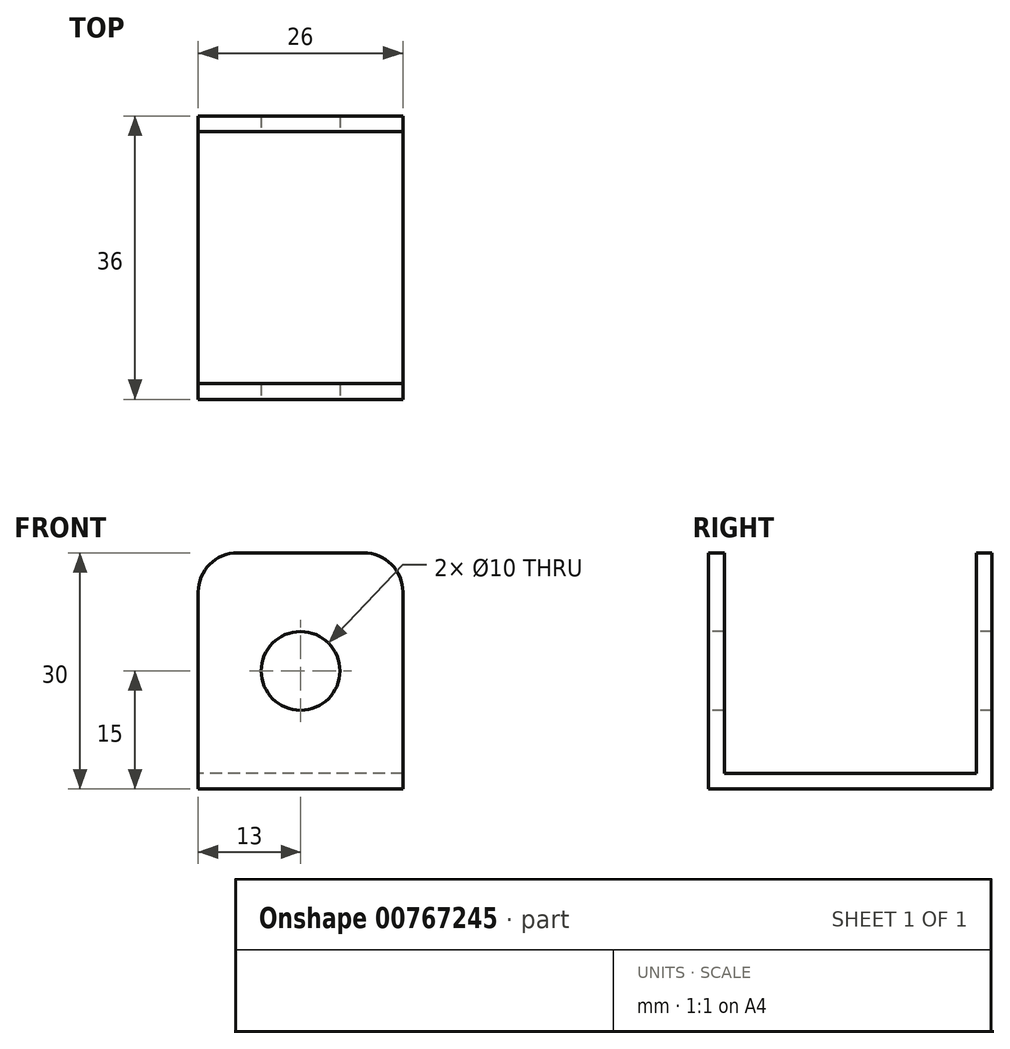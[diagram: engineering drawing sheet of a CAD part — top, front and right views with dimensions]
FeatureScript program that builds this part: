
annotation { "Feature Type Name" : "Feature", "Feature Type Description" : "" }
export const myFeature = defineFeature(function(context is Context, id is Id, definition is map)
    precondition{}
    {
        {
            var Q0;
            Q0=qCreatedBy(makeId("Right.planeOp"),FACE);
            var sketch = newSketch(context, id + "F0", { "sketchPlane" : qUnion([Q0])});
            skLineSegment(sketch, "E0.bottom", {"start": v(18, 15) * mm, "end": v(16, 15) * mm});
            skLineSegment(sketch, "E0.top", {"start": v(18, -15) * mm, "end": v(-18, -15) * mm});
            skLineSegment(sketch, "E0.left", {"start": v(18, 15) * mm, "end": v(18, -15) * mm});
            skLineSegment(sketch, "E0.right", {"start": v(-18, 15) * mm, "end": v(-18, -15) * mm});
            skPoint(sketch, "E0.middle", {"position": v(0, 0) * mm});
            skLineSegment(sketch, "E1.top", {"start": v(-16, -13) * mm, "end": v(16, -13) * mm});
            skLineSegment(sketch, "E1.left", {"start": v(-16, 15) * mm, "end": v(-16, -13) * mm});
            skLineSegment(sketch, "E1.right", {"start": v(16, 15) * mm, "end": v(16, -13) * mm});
            skLineSegment(sketch, "E2.trimOffspring", {"start": v(-16, 15) * mm, "end": v(-18, 15) * mm});
            skSolve(sketch);
        }
        {
            var Q0;
            Q0 = qSketchRegion(id + "F0", true);
            extrude(context, id + "F1", {"entities" : qUnion([Q0]), "endBound" : BoundingType.SYMMETRIC, "depth" : 26 * mm, "offsetDistance" : 25 * mm});
        }
        {
            var Q0;
            Q0=makeQuery(id+"F1.opExtrude","SWEPT_FACE",FACE,{"disambiguationData":[OSD([sQuery(id+"F0.wireOp",EDGE,"E0.right")])]});
            var sketch = newSketch(context, id + "F2", { "sketchPlane" : qUnion([Q0])});
            skCircle(sketch, "E3", {"center": v(0, 0) * mm, "radius": 5 * mm});
            skSolve(sketch);
        }
        {
            var Q0;
            Q0=makeQuery(id+"F2.imprint","IMPRINT",FACE,{"disambiguationData":[TD([[makeQuery(id+"F2.imprint","IMPRINT",EDGE,{"derivedFrom":sQuery(id+"F2.wireOp",EDGE,"E3")}),1.0]])]});
            extrude(context, id + "F3", {"entities" : qUnion([Q0]), "operationType" : NewBodyOperationType.REMOVE, "endBound" : BoundingType.THROUGH_ALL, "oppositeDirection" : true, "depth" : 25 * mm, "offsetDistance" : 25 * mm});
        }
        {
            var Q0;
            Q0=makeQuery(id+"F1.opExtrude","CAP_EDGE",EDGE,{"disambiguationData":[OSD([sQuery(id+"F0.wireOp",EDGE,"E2.trimOffspring")])],"isStart":false});
            var Q1;
            Q1=makeQuery(id+"F1.opExtrude","CAP_EDGE",EDGE,{"disambiguationData":[OSD([sQuery(id+"F0.wireOp",EDGE,"E2.trimOffspring")])],"isStart":true});
            var Q2;
            Q2=makeQuery(id+"F1.opExtrude","CAP_EDGE",EDGE,{"disambiguationData":[OSD([sQuery(id+"F0.wireOp",EDGE,"E0.bottom")])],"isStart":false});
            var Q3;
            Q3=makeQuery(id+"F1.opExtrude","CAP_EDGE",EDGE,{"disambiguationData":[OSD([sQuery(id+"F0.wireOp",EDGE,"E0.bottom")])],"isStart":true});
            fillet(context, id + "F4", {"entities" : qUnion([Q0, Q1, Q2, Q3]), "radius" : 5 * mm, "tangentPropagation" : true, "allowEdgeOverflow" : false});
        }
    });
